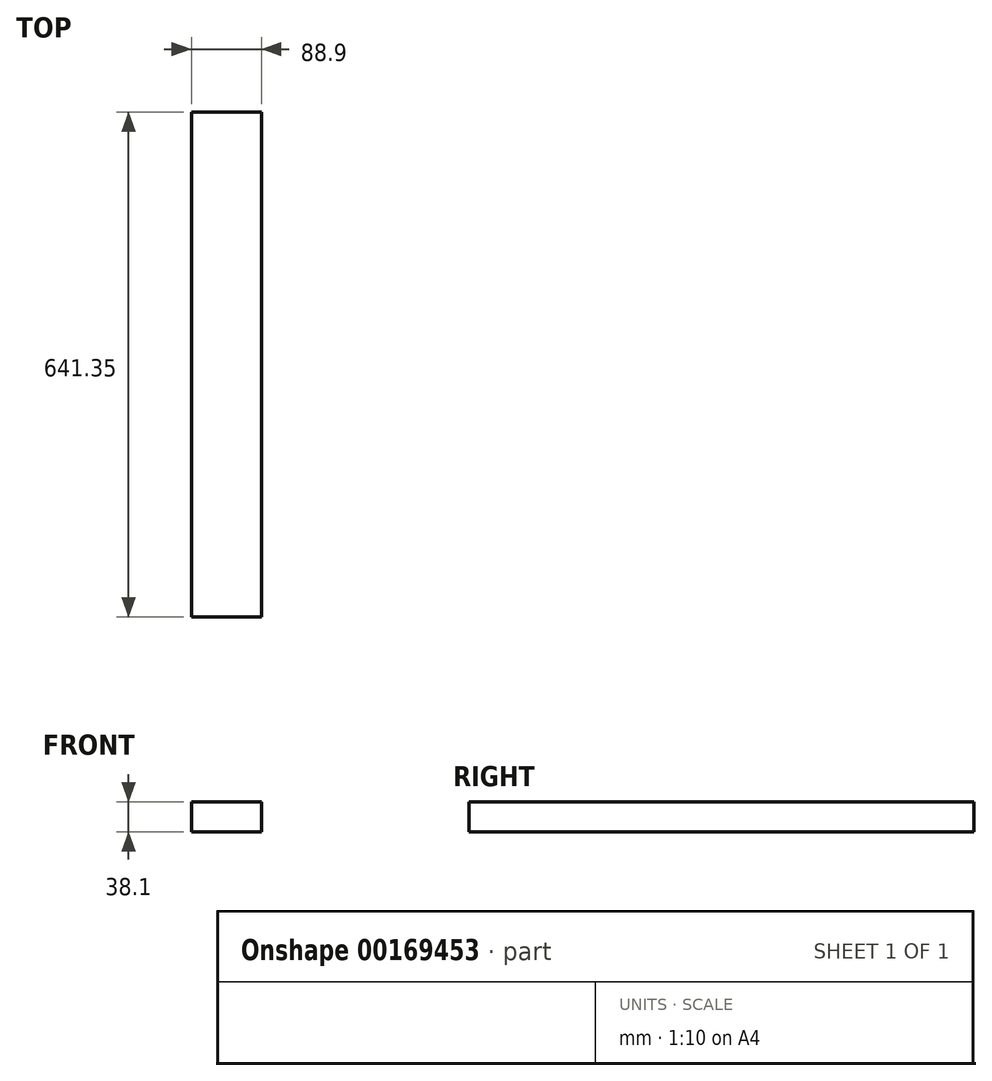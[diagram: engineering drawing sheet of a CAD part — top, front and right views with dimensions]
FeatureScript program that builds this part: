
annotation { "Feature Type Name" : "Feature", "Feature Type Description" : "" }
export const myFeature = defineFeature(function(context is Context, id is Id, definition is map)
    precondition{}
    {
        {
            var Q0;
            Q0=qCreatedBy(makeId("Front.planeOp"),FACE);
            var sketch = newSketch(context, id + "F0", { "sketchPlane" : qUnion([Q0])});
            skLineSegment(sketch, "E0.bottom", {"start": v(0, 0) * mm, "end": v(88.9, 0) * mm});
            skLineSegment(sketch, "E0.top", {"start": v(0, -38.1) * mm, "end": v(88.9, -38.1) * mm});
            skLineSegment(sketch, "E0.left", {"start": v(0, 0) * mm, "end": v(0, -38.1) * mm});
            skLineSegment(sketch, "E0.right", {"start": v(88.9, 0) * mm, "end": v(88.9, -38.1) * mm});
            skSolve(sketch);
        }
        {
            var Q0;
            Q0=qSketchRegion(id+"F0",true);
            extrude(context, id + "F1", {"entities" : qUnion([Q0]), "depth" : 641.35 * mm});
        }
    });
